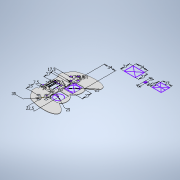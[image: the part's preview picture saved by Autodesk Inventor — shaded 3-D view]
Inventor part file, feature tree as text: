
AUTODESK INVENTOR PART (.ipt)
format: ipt  version: 2022 (Build 260153000, 153)  size: 253,440 bytes
history: native  units: mm
features: sketch x2, extrude x1
ambient origin geometry x8: Origin, YZ Plane, XZ Plane, XY Plane, X Axis, Y Axis, Z Axis, Center Point
bodies: Solid1 (feature_tree)
feature tree (3):
  sketch  "Sketch1"  dims[d0=35.0mm d1=60.0mm]
  extrude  "Extrusion1"  Depth=60.0mm
  sketch  "Sketch2"  dims[d2=17.5mm d3=25.0mm d4=22.5mm d6=25.0mm d7=27.0mm d8=34.0mm d9=27.0mm d10=7.5mm d11=25.0mm d12=27.0mm d13=34.0mm d14=27.0mm d15=6.0mm d16=6.0mm d17=6.0mm d18=6.5mm d22=6.0mm d23=40.0mm d25=360.0deg d27=25.0mm d28=27.0mm d31=40.0mm d32=25.0mm d33=27.0mm d34=5.0mm d35=8.0mm d36=8.0mm d37=35.0mm d38=8.0mm d39=12.0mm d40=8.0mm d41=60.0mm d42=17.5mm d47=4.0mm d48=7.5mm d49=22.5mm d50=25.0mm d51=27.0mm d52=34.0mm d53=6.5mm d54=3.0mm d55=3.0mm d56=6.0mm d57=6.0mm d58=40.0mm d60=360.0deg d62=50.0mm d63=1.0mm d64=0.0mm d65=1.5mm d66=12.5mm d67=27.0mm d68=25.0mm d69=1.401mm d70=13.425896mm d71=200.0mm d72=37.3mm d73=4.0mm d74=37.3mm]
